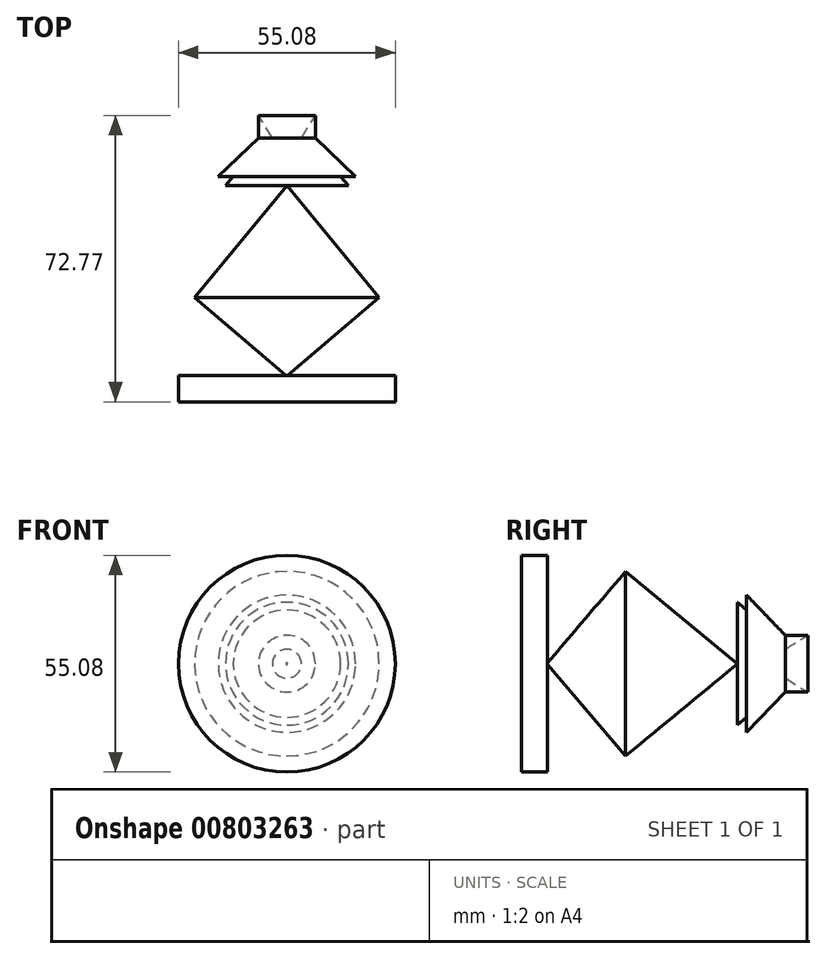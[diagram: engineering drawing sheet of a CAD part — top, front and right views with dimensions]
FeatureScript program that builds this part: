
annotation { "Feature Type Name" : "Feature", "Feature Type Description" : "" }
export const myFeature = defineFeature(function(context is Context, id is Id, definition is map)
    precondition{}
    {
        {
            var Q0;
            Q0=qCreatedBy(makeId("Top.planeOp"),FACE);
            var sketch = newSketch(context, id + "F0", { "sketchPlane" : qUnion([Q0])});
            skLineSegment(sketch, "E0", {"start": v(0, 75.47) * mm, "end": v(0, 0) * mm, "construction": true});
            skLineSegment(sketch, "E1", {"start": v(0, 0) * mm, "end": v(0, -76.58) * mm, "construction": true});
            skLineSegment(sketch, "E2.bottom", {"start": v(0, -54.89) * mm, "end": v(27.54, -54.89) * mm});
            skLineSegment(sketch, "E2.top", {"start": v(0, -48.2) * mm, "end": v(27.54, -48.2) * mm});
            skLineSegment(sketch, "E2.left", {"start": v(0, -54.89) * mm, "end": v(0, -48.2) * mm});
            skLineSegment(sketch, "E2.right", {"start": v(27.54, -54.89) * mm, "end": v(27.54, -48.2) * mm});
            skLineSegment(sketch, "E3", {"start": v(0, -48.2) * mm, "end": v(23.46, -28.56) * mm});
            skLineSegment(sketch, "E4", {"start": v(23.46, -28.56) * mm, "end": v(0, 0) * mm});
            skLineSegment(sketch, "E5", {"start": v(0, 0) * mm, "end": v(15.67, 0) * mm});
            skLineSegment(sketch, "E6", {"start": v(15.67, 0) * mm, "end": v(13.6, 2.51) * mm});
            skLineSegment(sketch, "E7", {"start": v(13.6, 2.51) * mm, "end": v(17.52, 2.51) * mm});
            skLineSegment(sketch, "E8", {"start": v(17.52, 2.51) * mm, "end": v(7.14, 12.05) * mm});
            skLineSegment(sketch, "E9", {"start": v(7.14, 12.05) * mm, "end": v(7.14, 17.99) * mm});
            skLineSegment(sketch, "E10", {"start": v(7.14, 17.99) * mm, "end": v(3.62, 12.05) * mm});
            skLineSegment(sketch, "E11", {"start": v(3.62, 12.05) * mm, "end": v(0, 12.05) * mm});
            skSolve(sketch);
        }
        {
            var Q0;
            Q0=makeQuery(id+"F0.imprint","IMPRINT",FACE,{"disambiguationData":[TD([[makeQuery(id+"F0.imprint","IMPRINT",EDGE,{"derivedFrom":sQuery(id+"F0.wireOp",EDGE,"E2.bottom")}),1.0]])]});
            var sketch = newSketch(context, id + "F1", { "sketchPlane" : qUnion([Q0])});
            skLineSegment(sketch, "E12", {"start": v(0, 0) * mm, "end": v(0, -48.4) * mm});
            skLineSegment(sketch, "E13", {"start": v(0, 0) * mm, "end": v(0, 12.05) * mm});
            skLineSegment(sketch, "E14", {"start": v(0, 0) * mm, "end": v(23.46, -28.37) * mm});
            skLineSegment(sketch, "E15", {"start": v(23.46, -28.37) * mm, "end": v(0, -48.4) * mm});
            skLineSegment(sketch, "E16", {"start": v(0, 0) * mm, "end": v(15.6, 0) * mm});
            skLineSegment(sketch, "E17", {"start": v(13.64, 2.34) * mm, "end": v(15.6, 0) * mm});
            skLineSegment(sketch, "E18", {"start": v(13.64, 2.34) * mm, "end": v(17.44, 2.34) * mm});
            skLineSegment(sketch, "E19", {"start": v(17.44, 2.34) * mm, "end": v(7.21, 12.17) * mm});
            skLineSegment(sketch, "E20", {"start": v(7.21, 12.17) * mm, "end": v(7.21, 17.88) * mm});
            skLineSegment(sketch, "E21", {"start": v(7.21, 17.88) * mm, "end": v(3.67, 12.17) * mm});
            skLineSegment(sketch, "E22", {"start": v(3.67, 12.17) * mm, "end": v(0, 12.05) * mm});
            skSolve(sketch);
        }
        {
            var Q0;
            {var subQ3=sQuery(id+"F1.wireOp",EDGE,"E14");Q0=makeQuery(id+"F1.imprint","IMPRINT",FACE,{"disambiguationData":[TD([[makeQuery(id+"F1.imprint","IMPRINT",EDGE,{"derivedFrom":subQ3}),-1.0]])]});}
            var Q1;
            Q1=makeQuery(id+"F1.imprint","IMPRINT",FACE,{"disambiguationData":[TD([[makeQuery(id+"F1.imprint","IMPRINT",EDGE,{"derivedFrom":sQuery(id+"F1.wireOp",EDGE,"E13")}),-1.0]])]});
            var Q2;
            Q2=makeQuery(id+"F0.imprint","IMPRINT",FACE,{"disambiguationData":[TD([[makeQuery(id+"F0.imprint","IMPRINT",EDGE,{"derivedFrom":sQuery(id+"F0.wireOp",EDGE,"E2.bottom")}),1.0]])]});
            var Q3;
            Q3=sQuery(id+"F0.wireOp",EDGE,"E0");
            revolve(context, id + "F2", {"surfaceOperationType" : NewSurfaceOperationType.NEW, "entities" : qUnion([Q0, Q1, Q2]), "axis" : qUnion([Q3]), "revolveType" : RevolveType.FULL});
        }
    });
